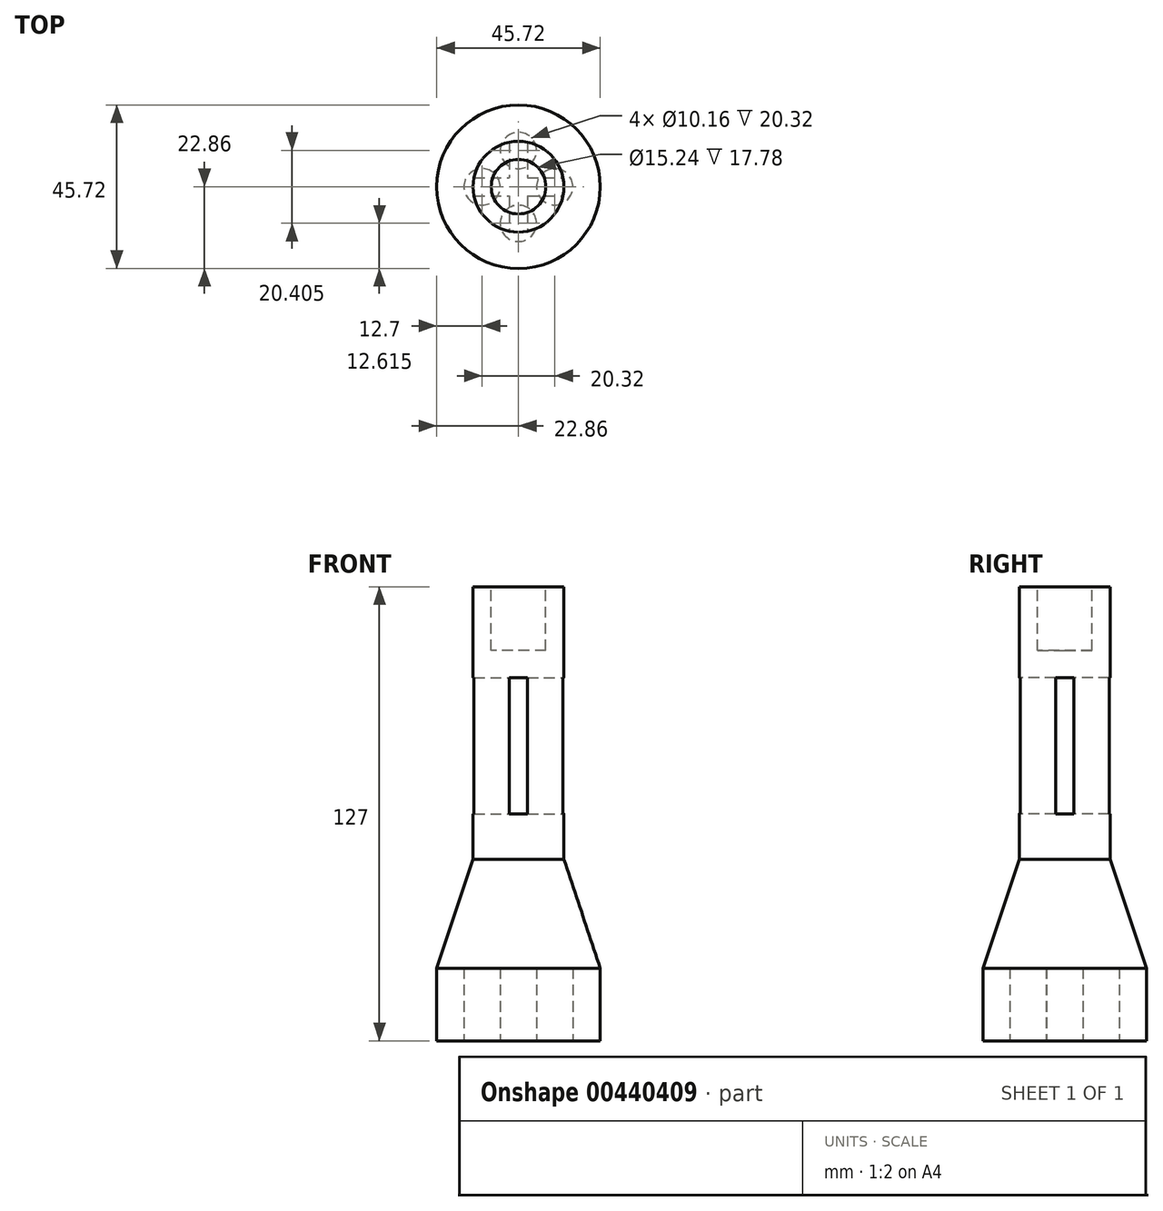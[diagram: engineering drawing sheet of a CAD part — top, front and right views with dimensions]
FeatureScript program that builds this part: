
annotation { "Feature Type Name" : "Feature", "Feature Type Description" : "" }
export const myFeature = defineFeature(function(context is Context, id is Id, definition is map)
    precondition{}
    {
        {
            var Q0;
            Q0=qCreatedBy(makeId("Front.planeOp"),FACE);
            var sketch = newSketch(context, id + "F0", { "sketchPlane" : qUnion([Q0])});
            skLineSegment(sketch, "E0", {"start": v(0, 0) * mm, "end": v(0, 63.5) * mm});
            skLineSegment(sketch, "E1", {"start": v(0, 63.5) * mm, "end": v(0, 50.8) * mm});
            skLineSegment(sketch, "E2", {"start": v(0, 0) * mm, "end": v(-22.86, 0) * mm});
            skLineSegment(sketch, "E3", {"start": v(-22.86, 0) * mm, "end": v(-22.86, 20.32) * mm});
            skLineSegment(sketch, "E4", {"start": v(-22.86, 20.32) * mm, "end": v(-12.7, 50.8) * mm});
            skLineSegment(sketch, "E5", {"start": v(-12.7, 50.8) * mm, "end": v(-12.7, 63.5) * mm});
            skLineSegment(sketch, "E6", {"start": v(-12.7, 63.5) * mm, "end": v(-12.7, 127) * mm});
            skLineSegment(sketch, "E7", {"start": v(-12.7, 127) * mm, "end": v(-7.62, 127) * mm});
            skLineSegment(sketch, "E8", {"start": v(-7.62, 127) * mm, "end": v(-7.62, 109.22) * mm});
            skLineSegment(sketch, "E9", {"start": v(-7.62, 109.22) * mm, "end": v(0, 109.22) * mm});
            skLineSegment(sketch, "E10", {"start": v(0, 109.22) * mm, "end": v(0, 63.5) * mm});
            skSolve(sketch);
        }
        {
            var Q0;
            Q0 = qSketchRegion(id + "F0", true);
            var Q1;
            Q1=sQuery(id+"F0.wireOp",EDGE,"E10");
            revolve(context, id + "F1", {"entities" : qUnion([Q0]), "axis" : qUnion([Q1]), "revolveType" : RevolveType.FULL});
        }
        {
            var Q0;
            Q0=qCreatedBy(makeId("Top.planeOp"),FACE);
            var sketch = newSketch(context, id + "F2", { "sketchPlane" : qUnion([Q0])});
            skLineSegment(sketch, "E11", {"start": v(0, 0) * mm, "end": v(0, 5.08) * mm});
            skLineSegment(sketch, "E12", {"start": v(0, 5.08) * mm, "end": v(0, 10.16) * mm});
            skLineSegment(sketch, "E13", {"start": v(0, 10.16) * mm, "end": v(0, 0) * mm});
            skLineSegment(sketch, "E14", {"start": v(0, 0) * mm, "end": v(10.16, 0) * mm});
            skLineSegment(sketch, "E15", {"start": v(10.16, 0) * mm, "end": v(5.08, 0) * mm});
            skLineSegment(sketch, "E16", {"start": v(5.08, 0) * mm, "end": v(0, 0) * mm});
            skLineSegment(sketch, "E17", {"start": v(0, -0.09) * mm, "end": v(0, -10.25) * mm});
            skLineSegment(sketch, "E18", {"start": v(0, -10.25) * mm, "end": v(0, -5.17) * mm});
            skLineSegment(sketch, "E19", {"start": v(0, -5.17) * mm, "end": v(0, 0) * mm});
            skLineSegment(sketch, "E20", {"start": v(0, 0) * mm, "end": v(-10.16, 0) * mm});
            skLineSegment(sketch, "E21", {"start": v(-10.16, 0) * mm, "end": v(-5.08, 0) * mm});
            skLineSegment(sketch, "E22", {"start": v(-5.08, 0) * mm, "end": v(0, 0) * mm});
            skCircle(sketch, "E23", {"center": v(0, 10.16) * mm, "radius": 5.08 * mm});
            skCircle(sketch, "E24", {"center": v(10.16, 0) * mm, "radius": 5.08 * mm});
            skCircle(sketch, "E25", {"center": v(0, -10.25) * mm, "radius": 5.08 * mm});
            skCircle(sketch, "E26", {"center": v(-10.16, 0) * mm, "radius": 5.08 * mm});
            skSolve(sketch);
        }
        {
            var Q0;
            Q0 = qSketchRegion(id + "F2", true);
            extrude(context, id + "F3", {"entities" : qUnion([Q0]), "operationType" : NewBodyOperationType.REMOVE, "depth" : 20.32 * mm});
        }
        {
            var Q0;
            Q0=qCreatedBy(makeId("Right.planeOp"),FACE);
            var sketch = newSketch(context, id + "F4", { "sketchPlane" : qUnion([Q0])});
            skLineSegment(sketch, "E27", {"start": v(0, 0) * mm, "end": v(0, 63.5) * mm});
            skLineSegment(sketch, "E28", {"start": v(0, 63.5) * mm, "end": v(2.54, 63.5) * mm});
            skLineSegment(sketch, "E29", {"start": v(2.54, 63.5) * mm, "end": v(2.54, 101.6) * mm});
            skLineSegment(sketch, "E30", {"start": v(2.54, 101.6) * mm, "end": v(-2.54, 101.6) * mm});
            skLineSegment(sketch, "E31", {"start": v(-2.54, 101.6) * mm, "end": v(-2.54, 63.5) * mm});
            skLineSegment(sketch, "E32", {"start": v(-2.54, 63.5) * mm, "end": v(0, 63.5) * mm});
            skSolve(sketch);
        }
        {
            var Q0;
            Q0 = qSketchRegion(id + "F4", true);
            extrude(context, id + "F5", {"entities" : qUnion([Q0]), "operationType" : NewBodyOperationType.REMOVE, "endBound" : BoundingType.SYMMETRIC, "oppositeDirection" : true, "depth" : 30.48 * mm});
        }
        {
            var Q0;
            Q0=qCreatedBy(makeId("Front.planeOp"),FACE);
            var sketch = newSketch(context, id + "F6", { "sketchPlane" : qUnion([Q0])});
            skLineSegment(sketch, "E33", {"start": v(0, 0) * mm, "end": v(0, 63.5) * mm});
            skLineSegment(sketch, "E34", {"start": v(0, 63.5) * mm, "end": v(-2.54, 63.5) * mm});
            skLineSegment(sketch, "E35", {"start": v(-2.54, 63.5) * mm, "end": v(-2.54, 101.6) * mm});
            skLineSegment(sketch, "E36", {"start": v(-2.54, 101.6) * mm, "end": v(2.54, 101.6) * mm});
            skLineSegment(sketch, "E37", {"start": v(2.54, 101.6) * mm, "end": v(2.54, 63.5) * mm});
            skLineSegment(sketch, "E38", {"start": v(2.54, 63.5) * mm, "end": v(0, 63.5) * mm});
            skSolve(sketch);
        }
        {
            var Q0;
            Q0 = qSketchRegion(id + "F6", true);
            extrude(context, id + "F7", {"entities" : qUnion([Q0]), "operationType" : NewBodyOperationType.REMOVE, "endBound" : BoundingType.SYMMETRIC, "oppositeDirection" : true, "depth" : 30.48 * mm});
        }
    });
